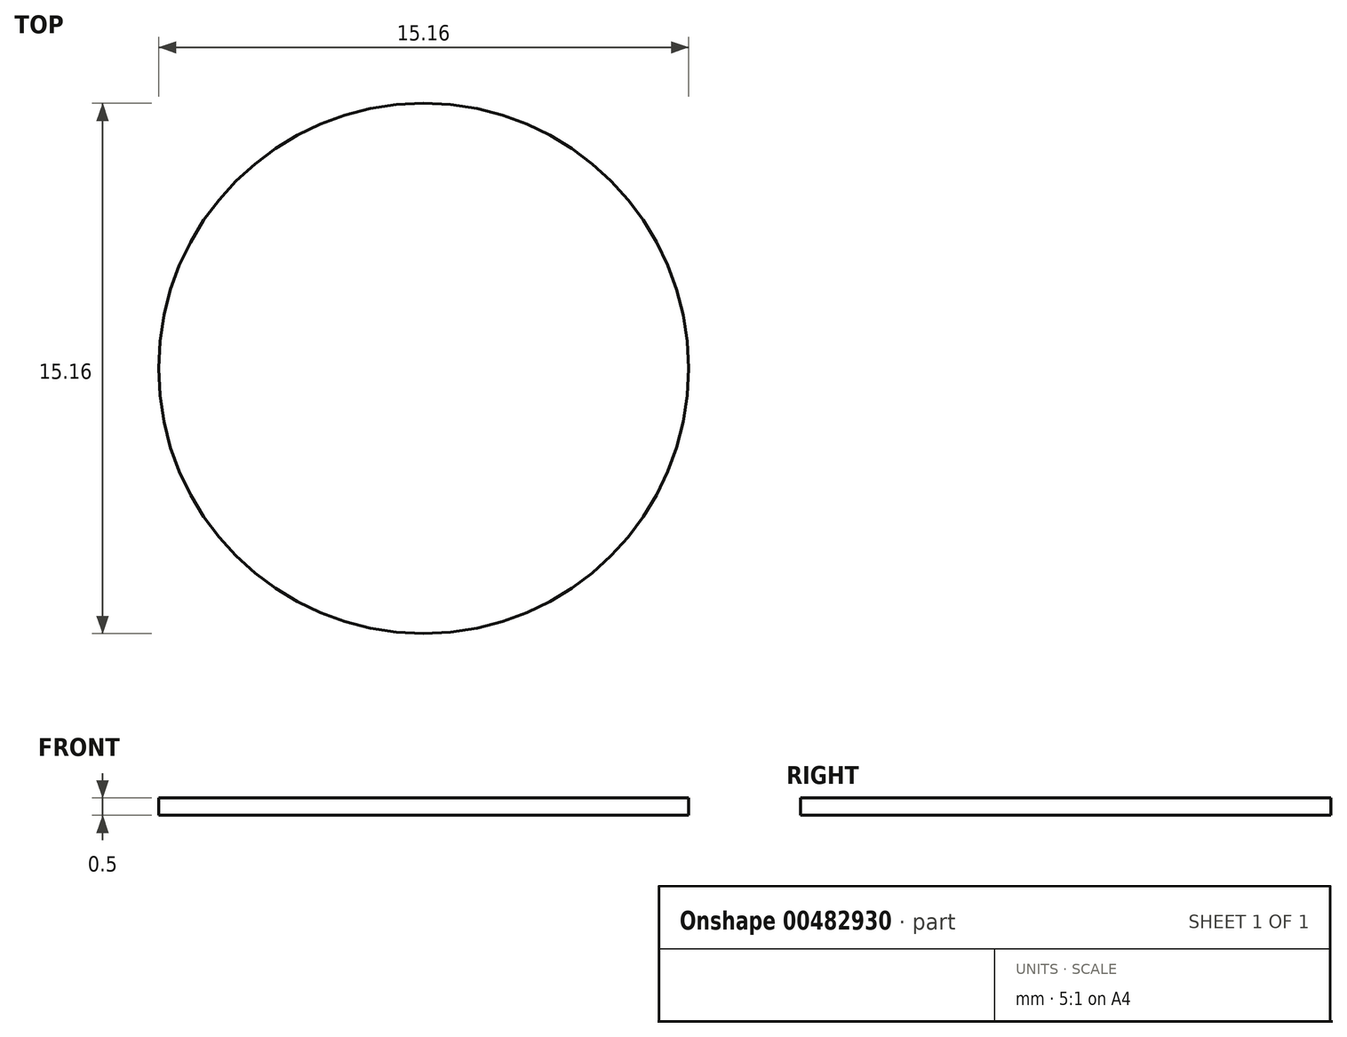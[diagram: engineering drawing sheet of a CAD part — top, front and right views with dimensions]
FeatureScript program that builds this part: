
annotation { "Feature Type Name" : "Feature", "Feature Type Description" : "" }
export const myFeature = defineFeature(function(context is Context, id is Id, definition is map)
    precondition{}
    {
        {
            var Q0;
            Q0=qCreatedBy(makeId("Top.planeOp"),FACE);
            var sketch = newSketch(context, id + "F0", { "sketchPlane" : qUnion([Q0])});
            skCircle(sketch, "E0", {"center": v(0, 0) * mm, "radius": 7.58 * mm});
            skSolve(sketch);
        }
        {
            var Q0;
            Q0=makeQuery(id+"F0.imprint","IMPRINT",FACE,{"disambiguationData":[TD([[makeQuery(id+"F0.imprint","IMPRINT",EDGE,{"derivedFrom":sQuery(id+"F0.wireOp",EDGE,"E0")}),1.0]])]});
            extrude(context, id + "F1", {"entities" : qUnion([Q0]), "depth" : 0.5 * mm});
        }
    });
